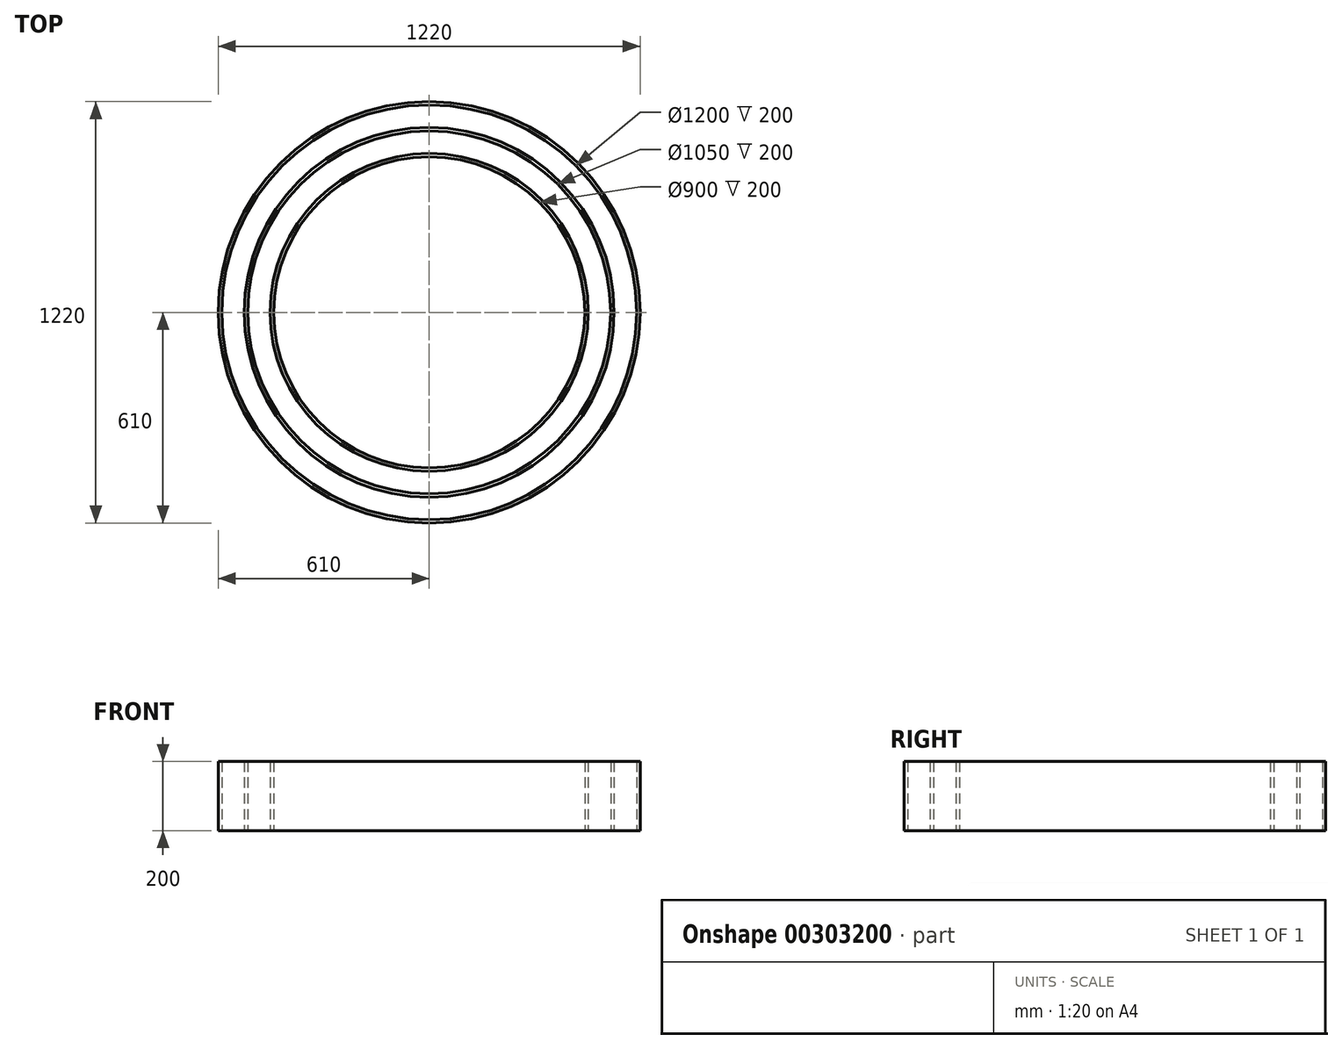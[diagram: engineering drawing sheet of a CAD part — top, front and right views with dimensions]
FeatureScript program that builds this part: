
annotation { "Feature Type Name" : "Feature", "Feature Type Description" : "" }
export const myFeature = defineFeature(function(context is Context, id is Id, definition is map)
    precondition{}
    {
        {
            var Q0;
            Q0=qCreatedBy(makeId("Top.planeOp"),FACE);
            var sketch = newSketch(context, id + "F0", { "sketchPlane" : qUnion([Q0])});
            skCircle(sketch, "E0", {"center": v(0, 0) * mm, "radius": 600 * mm});
            skCircle(sketch, "E1", {"center": v(0, 0) * mm, "radius": 610 * mm});
            skCircle(sketch, "E2", {"center": v(0, 0) * mm, "radius": 525 * mm});
            skCircle(sketch, "E3", {"center": v(0, 0) * mm, "radius": 535 * mm});
            skCircle(sketch, "E4", {"center": v(0, 0) * mm, "radius": 450 * mm});
            skCircle(sketch, "E5", {"center": v(0, 0) * mm, "radius": 460 * mm});
            skSolve(sketch);
        }
        {
            var Q0;
            Q0=makeQuery(id+"F0.imprint","IMPRINT",FACE,{"disambiguationData":[TD([[makeQuery(id+"F0.imprint","IMPRINT",EDGE,{"derivedFrom":sQuery(id+"F0.wireOp",EDGE,"E0")}),-1.0]])]});
            var Q1;
            Q1=makeQuery(id+"F0.imprint","IMPRINT",FACE,{"disambiguationData":[TD([[makeQuery(id+"F0.imprint","IMPRINT",EDGE,{"derivedFrom":sQuery(id+"F0.wireOp",EDGE,"E4")}),-1.0]])]});
            var Q2;
            Q2=makeQuery(id+"F0.imprint","IMPRINT",FACE,{"disambiguationData":[TD([[makeQuery(id+"F0.imprint","IMPRINT",EDGE,{"derivedFrom":sQuery(id+"F0.wireOp",EDGE,"E2")}),-1.0]])]});
            extrude(context, id + "F1", {"entities" : qUnion([Q0, Q1, Q2]), "depth" : 200 * mm});
        }
    });
